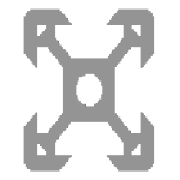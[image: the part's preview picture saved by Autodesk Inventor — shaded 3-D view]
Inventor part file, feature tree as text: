
AUTODESK INVENTOR PART (.ipt)
format: ipt  version: 2013 (Build 170138000, 138)  size: 193,024 bytes
history: native  units: mm
features: other x4, plane x2, sketch x2, split x1
ambient origin geometry x8: Origin, YZ Plane, XZ Plane, XY Plane, X Axis, Y Axis, Z Axis, Center Point
bodies: Solid1 (feature_tree), Body (feature_tree)
feature tree (9):
  other  "Driven Length"
  other  "Frame Generator"
  other  "Start Plane"
  other  "End Plane"
  plane  "Work Plane5"
  split  "Split1"
  sketch  "Sketch4"  dims[d2=4.2mm]
  plane  "Work Plane4"
  sketch  "Sketch5"  dims[d3=1.5mm d4=1.64mm d5=1.8mm d6=5.68mm d7=1.8mm d9=1.5mm d12=80.0mm d13=275.0mm d14=0.13mm d15=0.0mm d18=90.0deg d17=195.0mm]
